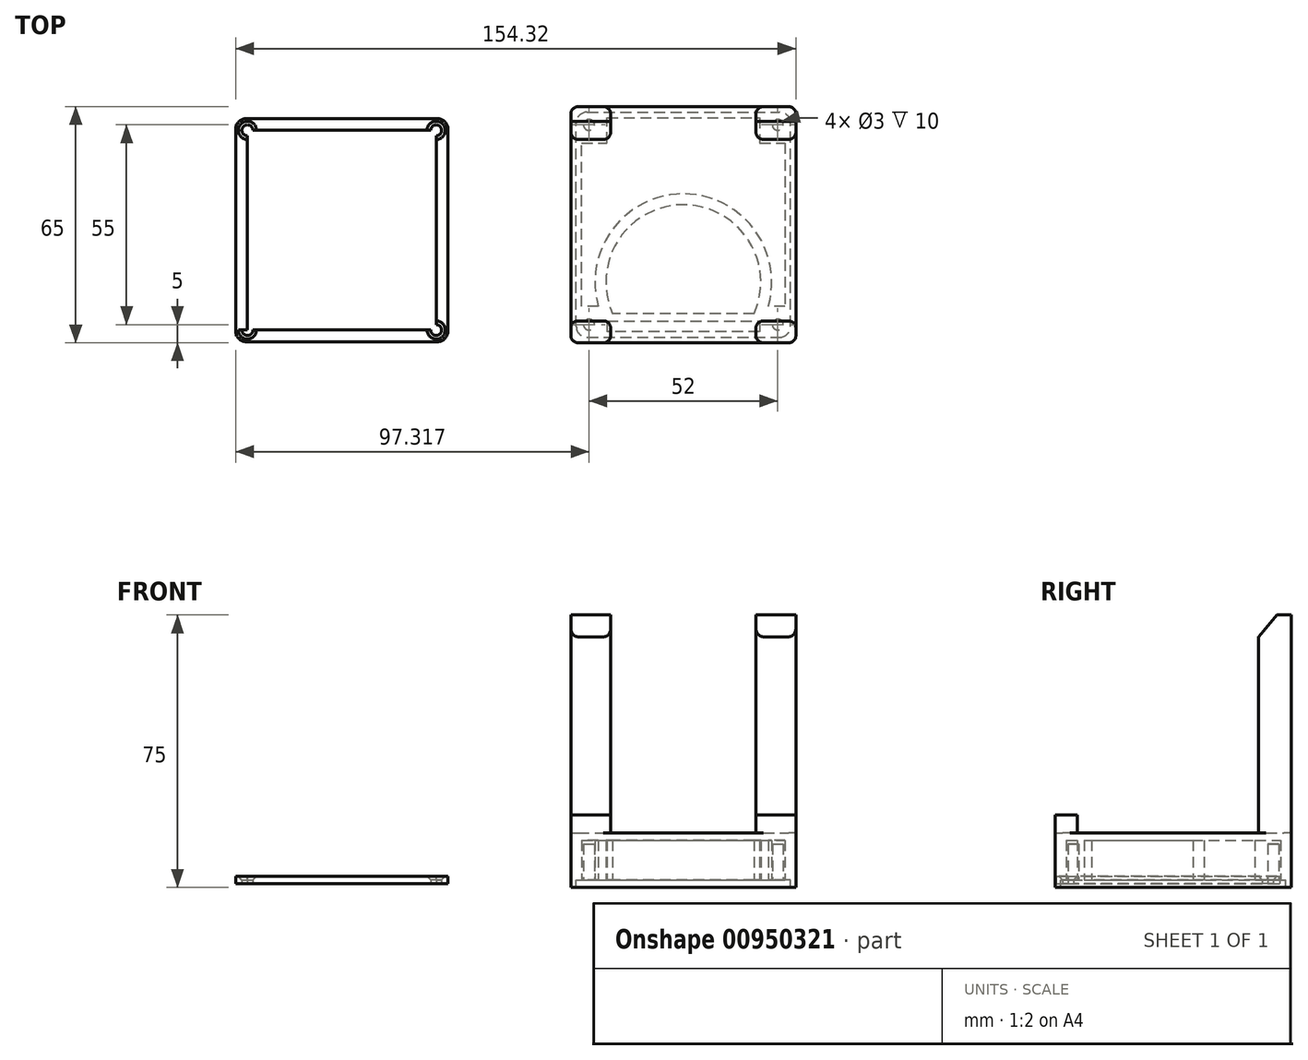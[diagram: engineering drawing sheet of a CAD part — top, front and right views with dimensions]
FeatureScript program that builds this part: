
annotation { "Feature Type Name" : "Feature", "Feature Type Description" : "" }
export const myFeature = defineFeature(function(context is Context, id is Id, definition is map)
    precondition{}
    {
        {
            var Q0;
            Q0=qCreatedBy(makeId("Top.planeOp"),FACE);
            var sketch = newSketch(context, id + "F0", { "sketchPlane" : qUnion([Q0])});
            skLineSegment(sketch, "E0.bottom", {"start": v(-55.57, -28) * mm, "end": v(-107.57, -28) * mm});
            skLineSegment(sketch, "E0.top", {"start": v(-55.57, 28) * mm, "end": v(-107.57, 28) * mm});
            skLineSegment(sketch, "E0.left", {"start": v(-50.57, -23) * mm, "end": v(-50.57, 23) * mm});
            skLineSegment(sketch, "E0.right", {"start": v(-112.57, -23) * mm, "end": v(-112.57, 23) * mm});
            skPoint(sketch, "E0.middle", {"position": v(-81.57, 0) * mm});
            skPoint(sketch, "E1.visualSharp", {"position": v(-112.57, 28) * mm});
            skPoint(sketch, "E2.visualSharp", {"position": v(-50.57, 28) * mm});
            skPoint(sketch, "E3.visualSharp", {"position": v(-50.57, -28) * mm});
            skPoint(sketch, "E4.visualSharp", {"position": v(-112.57, -28) * mm});
            skPoint(sketch, "E5", {"position": v(-81.57, -20) * mm});
            skPoint(sketch, "E5.positionSnap0", {"position": v(-81.57, -28) * mm});
            skPoint(sketch, "E6", {"position": v(-81.57, 10) * mm});
            skPoint(sketch, "E7", {"position": v(-101.07, -20) * mm});
            skPoint(sketch, "E8", {"position": v(-62.07, -20) * mm});
            skLineSegment(sketch, "E9", {"start": v(-101.07, -20) * mm, "end": v(-62.07, -20) * mm});
            skLineSegment(sketch, "E10", {"start": v(-81.57, 10) * mm, "end": v(-81.57, -20) * mm, "construction": true});
            skArc(sketch, "E11", {"start": v(-62.07, -20) * mm, "mid": v(-81.57, 10) * mm, "end": v(-101.07, -20) * mm});
            skLineSegment(sketch, "E12", {"start": v(-112.57, -23) * mm, "end": v(-112.57, -28) * mm});
            skLineSegment(sketch, "E13", {"start": v(-107.57, -28) * mm, "end": v(-112.57, -28) * mm});
            skLineSegment(sketch, "E14", {"start": v(-112.57, 23) * mm, "end": v(-112.57, 28) * mm});
            skLineSegment(sketch, "E15", {"start": v(-112.57, 28) * mm, "end": v(-107.57, 28) * mm});
            skLineSegment(sketch, "E16", {"start": v(-55.57, 28) * mm, "end": v(-50.57, 28) * mm});
            skLineSegment(sketch, "E17", {"start": v(-50.57, 28) * mm, "end": v(-50.57, 23) * mm});
            skLineSegment(sketch, "E18", {"start": v(-50.57, -23) * mm, "end": v(-50.57, -28) * mm});
            skLineSegment(sketch, "E19", {"start": v(-55.57, -28) * mm, "end": v(-50.57, -28) * mm});
            skArc(sketch, "E20.0", {"start": v(-60.21, -23) * mm, "mid": v(-81.57, 13) * mm, "end": v(-102.93, -23) * mm});
            skLineSegment(sketch, "E20.1", {"start": v(-102.93, -23) * mm, "end": v(-60.21, -23) * mm});
            skSolve(sketch);
        }
        {
            var Q0;
            Q0=makeQuery(id+"F0.imprint","IMPRINT",FACE,{"disambiguationData":[TD([[makeQuery(id+"F0.imprint","IMPRINT",EDGE,{"derivedFrom":sQuery(id+"F0.wireOp",EDGE,"E0.bottom")}),-1.0]])]});
            var Q1;
            Q1=makeQuery(id+"F0.imprint","IMPRINT",FACE,{"disambiguationData":[TD([[makeQuery(id+"F0.imprint","IMPRINT",EDGE,{"derivedFrom":sQuery(id+"F0.wireOp",EDGE,"E9")}),1.0]])]});
            var Q2;
            Q2=makeQuery(id+"F0.imprint","IMPRINT",FACE,{"disambiguationData":[TD([[makeQuery(id+"F0.imprint","IMPRINT",EDGE,{"derivedFrom":sQuery(id+"F0.wireOp",EDGE,"E9")}),-1.0]])]});
            extrude(context, id + "F1", {"entities" : qUnion([Q0, Q1, Q2]), "depth" : 14 * mm, "offsetDistance" : 25 * mm});
        }
        {
            var Q0;
            Q0=makeQuery(id+"F1.opExtrude","CAP_FACE",FACE,{"disambiguationData":[OSD([sQuery(id+"F0.wireOp",EDGE,"E0.bottom"),sQuery(id+"F0.wireOp",EDGE,"E0.top"),sQuery(id+"F0.wireOp",EDGE,"E0.left"),sQuery(id+"F0.wireOp",EDGE,"E0.right"),sQuery(id+"F0.wireOp",EDGE,"E12"),sQuery(id+"F0.wireOp",EDGE,"E13"),sQuery(id+"F0.wireOp",EDGE,"E14"),sQuery(id+"F0.wireOp",EDGE,"E15"),sQuery(id+"F0.wireOp",EDGE,"E16"),sQuery(id+"F0.wireOp",EDGE,"E17"),sQuery(id+"F0.wireOp",EDGE,"E18"),sQuery(id+"F0.wireOp",EDGE,"E19")])],"isStart":false});
            var sketch = newSketch(context, id + "F2", { "sketchPlane" : qUnion([Q0])});
            skLineSegment(sketch, "E21.bottom", {"start": v(-112.57, -28) * mm, "end": v(-101.57, -28) * mm});
            skLineSegment(sketch, "E21.top", {"start": v(-112.57, -25) * mm, "end": v(-101.57, -25) * mm});
            skLineSegment(sketch, "E21.left", {"start": v(-112.57, -28) * mm, "end": v(-112.57, -25) * mm});
            skLineSegment(sketch, "E21.right", {"start": v(-50.57, -28) * mm, "end": v(-50.57, -25) * mm});
            skLineSegment(sketch, "E22.bottom", {"start": v(-112.57, 28) * mm, "end": v(-101.57, 28) * mm});
            skLineSegment(sketch, "E22.top", {"start": v(-112.57, 25) * mm, "end": v(-101.57, 25) * mm});
            skLineSegment(sketch, "E22.left", {"start": v(-112.57, 28) * mm, "end": v(-112.57, 25) * mm});
            skLineSegment(sketch, "E22.right", {"start": v(-50.57, 28) * mm, "end": v(-50.57, 25) * mm});
            skPoint(sketch, "E23", {"position": v(-101.57, -25) * mm});
            skPoint(sketch, "E24", {"position": v(-61.57, -25) * mm});
            skPoint(sketch, "E25", {"position": v(-101.57, 25) * mm});
            skPoint(sketch, "E26", {"position": v(-61.57, 25) * mm});
            skLineSegment(sketch, "E27", {"start": v(-101.57, -25) * mm, "end": v(-101.57, -28) * mm});
            skLineSegment(sketch, "E28", {"start": v(-61.57, -25) * mm, "end": v(-61.57, -28) * mm});
            skLineSegment(sketch, "E29", {"start": v(-61.57, 25) * mm, "end": v(-61.57, 28) * mm});
            skLineSegment(sketch, "E30", {"start": v(-101.57, 25) * mm, "end": v(-101.57, 28) * mm});
            skLineSegment(sketch, "E31.trimOffspring", {"start": v(-61.57, -25) * mm, "end": v(-50.57, -25) * mm});
            skLineSegment(sketch, "E32.trimOffspring", {"start": v(-61.57, -28) * mm, "end": v(-50.57, -28) * mm});
            skLineSegment(sketch, "E33.trimOffspring", {"start": v(-61.57, 25) * mm, "end": v(-50.57, 25) * mm});
            skLineSegment(sketch, "E34.trimOffspring", {"start": v(-61.57, 28) * mm, "end": v(-50.57, 28) * mm});
            skSolve(sketch);
        }
        {
            var Q0;
            Q0=makeQuery(id+"F2.imprint","IMPRINT",FACE,{"disambiguationData":[TD([[makeQuery(id+"F2.imprint","IMPRINT",EDGE,{"derivedFrom":sQuery(id+"F2.wireOp",EDGE,"E21.bottom")}),-1.0]])]});
            var Q1;
            Q1=makeQuery(id+"F2.imprint","IMPRINT",FACE,{"disambiguationData":[TD([[makeQuery(id+"F2.imprint","IMPRINT",EDGE,{"derivedFrom":sQuery(id+"F2.wireOp",EDGE,"E21.right")}),-1.0]])]});
            extrude(context, id + "F3", {"entities" : qUnion([Q0, Q1]), "operationType" : NewBodyOperationType.ADD, "depth" : 5 * mm, "offsetDistance" : 25 * mm});
        }
        {
            var Q0;
            Q0=makeQuery(id+"F2.imprint","IMPRINT",FACE,{"disambiguationData":[TD([[makeQuery(id+"F2.imprint","IMPRINT",EDGE,{"derivedFrom":sQuery(id+"F2.wireOp",EDGE,"E22.bottom")}),-1.0]])]});
            var Q1;
            Q1=makeQuery(id+"F2.imprint","IMPRINT",FACE,{"disambiguationData":[TD([[makeQuery(id+"F2.imprint","IMPRINT",EDGE,{"derivedFrom":sQuery(id+"F2.wireOp",EDGE,"E22.right")}),-1.0]])]});
            extrude(context, id + "F4", {"entities" : qUnion([Q0, Q1]), "operationType" : NewBodyOperationType.ADD, "depth" : 60 * mm, "offsetDistance" : 25 * mm});
        }
        {
            var Q0;
            Q0=makeQuery(id+"F3.boolean.opBoolean","MERGE",FACE,{"derivedFrom":[makeQuery(id+"F1.opExtrude","SWEPT_FACE",FACE,{"disambiguationData":[OSD([sQuery(id+"F0.wireOp",EDGE,"E0.bottom"),sQuery(id+"F0.wireOp",EDGE,"E13"),sQuery(id+"F0.wireOp",EDGE,"E19")])]}),makeQuery(id+"F3.opExtrude","SWEPT_FACE",FACE,{"disambiguationData":[OSD([sQuery(id+"F2.wireOp",EDGE,"E21.bottom")])]}),makeQuery(id+"F3.opExtrude","SWEPT_FACE",FACE,{"disambiguationData":[OSD([sQuery(id+"F2.wireOp",EDGE,"E32.trimOffspring")])]})]});
            extrude(context, id + "F5", {"entities" : qUnion([Q0]), "operationType" : NewBodyOperationType.ADD, "depth" : 3 * mm, "offsetDistance" : 25 * mm});
        }
        {
            var Q0;
            Q0=makeQuery(id+"F4.boolean.opBoolean","MERGE",FACE,{"derivedFrom":[makeQuery(id+"F1.opExtrude","SWEPT_FACE",FACE,{"disambiguationData":[OSD([sQuery(id+"F0.wireOp",EDGE,"E0.top"),sQuery(id+"F0.wireOp",EDGE,"E15"),sQuery(id+"F0.wireOp",EDGE,"E16")])]}),makeQuery(id+"F4.opExtrude","SWEPT_FACE",FACE,{"disambiguationData":[OSD([sQuery(id+"F2.wireOp",EDGE,"E22.bottom")])]}),makeQuery(id+"F4.opExtrude","SWEPT_FACE",FACE,{"disambiguationData":[OSD([sQuery(id+"F2.wireOp",EDGE,"E34.trimOffspring")])]})]});
            extrude(context, id + "F6", {"entities" : qUnion([Q0]), "operationType" : NewBodyOperationType.ADD, "depth" : 6 * mm, "offsetDistance" : 25 * mm});
        }
        {
            var Q0;
            Q0=makeQuery(id+"F6.opExtrude","CAP_EDGE",EDGE,{"disambiguationData":[OSD([sQuery(id+"F0.wireOp",EDGE,"E16"),sQuery(id+"F0.wireOp",EDGE,"E17"),sQuery(id+"F2.wireOp",EDGE,"E22.right"),sQuery(id+"F2.wireOp",EDGE,"E34.trimOffspring")])],"isStart":false});
            var Q1;
            Q1=makeQuery(id+"F6.opExtrude","CAP_EDGE",EDGE,{"disambiguationData":[OSD([sQuery(id+"F0.wireOp",EDGE,"E0.top"),sQuery(id+"F0.wireOp",EDGE,"E15"),sQuery(id+"F0.wireOp",EDGE,"E16"),sQuery(id+"F2.wireOp",EDGE,"E29"),sQuery(id+"F2.wireOp",EDGE,"E34.trimOffspring")])],"isStart":false});
            var Q2;
            Q2=makeQuery(id+"F6.opExtrude","CAP_EDGE",EDGE,{"disambiguationData":[OSD([sQuery(id+"F0.wireOp",EDGE,"E0.top"),sQuery(id+"F0.wireOp",EDGE,"E15"),sQuery(id+"F0.wireOp",EDGE,"E16"),sQuery(id+"F2.wireOp",EDGE,"E22.bottom"),sQuery(id+"F2.wireOp",EDGE,"E30")])],"isStart":false});
            var Q3;
            Q3=makeQuery(id+"F6.opExtrude","CAP_EDGE",EDGE,{"disambiguationData":[OSD([sQuery(id+"F0.wireOp",EDGE,"E14"),sQuery(id+"F0.wireOp",EDGE,"E15"),sQuery(id+"F2.wireOp",EDGE,"E22.bottom"),sQuery(id+"F2.wireOp",EDGE,"E22.left")])],"isStart":false});
            var Q4;
            Q4=makeQuery(id+"F5.opExtrude","CAP_EDGE",EDGE,{"disambiguationData":[OSD([sQuery(id+"F0.wireOp",EDGE,"E18"),sQuery(id+"F0.wireOp",EDGE,"E19"),sQuery(id+"F2.wireOp",EDGE,"E21.right"),sQuery(id+"F2.wireOp",EDGE,"E32.trimOffspring")])],"isStart":false});
            var Q5;
            Q5=makeQuery(id+"F5.opExtrude","CAP_EDGE",EDGE,{"disambiguationData":[OSD([sQuery(id+"F0.wireOp",EDGE,"E12"),sQuery(id+"F0.wireOp",EDGE,"E13"),sQuery(id+"F2.wireOp",EDGE,"E21.bottom"),sQuery(id+"F2.wireOp",EDGE,"E21.left")])],"isStart":false});
            var Q6;
            Q6=makeQuery(id+"F5.opExtrude","CAP_EDGE",EDGE,{"disambiguationData":[OSD([sQuery(id+"F0.wireOp",EDGE,"E0.bottom"),sQuery(id+"F0.wireOp",EDGE,"E13"),sQuery(id+"F0.wireOp",EDGE,"E19"),sQuery(id+"F2.wireOp",EDGE,"E21.bottom"),sQuery(id+"F2.wireOp",EDGE,"E27")])],"isStart":false});
            var Q7;
            Q7=makeQuery(id+"F5.opExtrude","CAP_EDGE",EDGE,{"disambiguationData":[OSD([sQuery(id+"F0.wireOp",EDGE,"E0.bottom"),sQuery(id+"F0.wireOp",EDGE,"E13"),sQuery(id+"F0.wireOp",EDGE,"E19"),sQuery(id+"F2.wireOp",EDGE,"E28"),sQuery(id+"F2.wireOp",EDGE,"E32.trimOffspring")])],"isStart":false});
            fillet(context, id + "F7", {"entities" : qUnion([Q0, Q1, Q2, Q3, Q4, Q5, Q6, Q7]), "radius" : 2 * mm, "tangentPropagation" : true, "allowEdgeOverflow" : false});
        }
        {
            var Q0;
            Q0=makeQuery(id+"F3.opExtrude","SWEPT_EDGE",EDGE,{"disambiguationData":[OSD([sQuery(id+"F2.wireOp",EDGE,"E21.top"),sQuery(id+"F2.wireOp",EDGE,"E27")])]});
            var Q1;
            Q1=makeQuery(id+"F3.opExtrude","SWEPT_EDGE",EDGE,{"disambiguationData":[OSD([sQuery(id+"F0.wireOp",EDGE,"E0.right"),sQuery(id+"F0.wireOp",EDGE,"E12"),sQuery(id+"F0.wireOp",EDGE,"E14"),sQuery(id+"F2.wireOp",EDGE,"E21.top"),sQuery(id+"F2.wireOp",EDGE,"E21.left")])]});
            var Q2;
            Q2=makeQuery(id+"F3.opExtrude","SWEPT_EDGE",EDGE,{"disambiguationData":[OSD([sQuery(id+"F2.wireOp",EDGE,"E28"),sQuery(id+"F2.wireOp",EDGE,"E31.trimOffspring")])]});
            var Q3;
            Q3=makeQuery(id+"F3.opExtrude","SWEPT_EDGE",EDGE,{"disambiguationData":[OSD([sQuery(id+"F0.wireOp",EDGE,"E0.left"),sQuery(id+"F0.wireOp",EDGE,"E17"),sQuery(id+"F0.wireOp",EDGE,"E18"),sQuery(id+"F2.wireOp",EDGE,"E21.right"),sQuery(id+"F2.wireOp",EDGE,"E31.trimOffspring")])]});
            fillet(context, id + "F8", {"entities" : qUnion([Q0, Q1, Q2, Q3]), "radius" : 2 * mm, "tangentPropagation" : true, "allowEdgeOverflow" : false});
        }
        {
            var Q0;
            Q0=makeQuery(id+"F4.opExtrude","CAP_EDGE",EDGE,{"disambiguationData":[OSD([sQuery(id+"F2.wireOp",EDGE,"E22.top")])],"isStart":false});
            var Q1;
            Q1=makeQuery(id+"F4.opExtrude","CAP_EDGE",EDGE,{"disambiguationData":[OSD([sQuery(id+"F2.wireOp",EDGE,"E33.trimOffspring")])],"isStart":false});
            chamfer(context, id + "F9", {"entities" : qUnion([Q0, Q1]), "chamferType" : ChamferType.TWO_OFFSETS, "width1" : 5 * mm, "oppositeDirection" : false, "width2" : 6 * mm, "tangentPropagation" : true});
        }
        {
            var Q0;
            Q0=makeQuery(id+"F4.opExtrude","SWEPT_EDGE",EDGE,{"disambiguationData":[OSD([sQuery(id+"F2.wireOp",EDGE,"E22.top"),sQuery(id+"F2.wireOp",EDGE,"E30")])]});
            var Q1;
            Q1=makeQuery(id+"F4.opExtrude","SWEPT_EDGE",EDGE,{"disambiguationData":[OSD([sQuery(id+"F0.wireOp",EDGE,"E0.right"),sQuery(id+"F0.wireOp",EDGE,"E12"),sQuery(id+"F0.wireOp",EDGE,"E14"),sQuery(id+"F2.wireOp",EDGE,"E22.top"),sQuery(id+"F2.wireOp",EDGE,"E22.left")])]});
            var Q2;
            Q2=makeQuery(id+"F4.opExtrude","SWEPT_EDGE",EDGE,{"disambiguationData":[OSD([sQuery(id+"F2.wireOp",EDGE,"E29"),sQuery(id+"F2.wireOp",EDGE,"E33.trimOffspring")])]});
            var Q3;
            Q3=makeQuery(id+"F4.opExtrude","SWEPT_EDGE",EDGE,{"disambiguationData":[OSD([sQuery(id+"F0.wireOp",EDGE,"E0.left"),sQuery(id+"F0.wireOp",EDGE,"E17"),sQuery(id+"F0.wireOp",EDGE,"E18"),sQuery(id+"F2.wireOp",EDGE,"E22.right"),sQuery(id+"F2.wireOp",EDGE,"E33.trimOffspring")])]});
            fillet(context, id + "F10", {"entities" : qUnion([Q0, Q1, Q2, Q3]), "radius" : 2 * mm, "tangentPropagation" : true, "allowEdgeOverflow" : false});
        }
        {
            var Q0;
            {var subQ0=sQuery(id+"F0.wireOp",EDGE,"E16");var subQ1=sQuery(id+"F0.wireOp",EDGE,"E15");var subQ2=sQuery(id+"F0.wireOp",EDGE,"E0.top");var subQ3=sQuery(id+"F0.wireOp",EDGE,"E19");var subQ4=sQuery(id+"F0.wireOp",EDGE,"E13");var subQ5=sQuery(id+"F0.wireOp",EDGE,"E0.bottom");Q0=makeQuery(id+"F6.boolean.opBoolean","MERGE",FACE,{"derivedFrom":[makeQuery(id+"F5.boolean.opBoolean","MERGE",FACE,{"derivedFrom":[makeQuery(id+"F1.opExtrude","CAP_FACE",FACE,{"disambiguationData":[OSD([subQ5,subQ2,sQuery(id+"F0.wireOp",EDGE,"E0.left"),sQuery(id+"F0.wireOp",EDGE,"E0.right"),sQuery(id+"F0.wireOp",EDGE,"E12"),subQ4,sQuery(id+"F0.wireOp",EDGE,"E14"),subQ1,subQ0,sQuery(id+"F0.wireOp",EDGE,"E17"),sQuery(id+"F0.wireOp",EDGE,"E18"),subQ3])],"isStart":true}),makeQuery(id+"F5.opExtrude","SWEPT_FACE",FACE,{"disambiguationData":[OSD([subQ5,subQ4,subQ3]),TDD([makeQuery(id+"F1.opExtrude","CAP_EDGE",EDGE,{"disambiguationData":[OSD([subQ5,subQ4,subQ3])],"isStart":true})])]})]}),makeQuery(id+"F6.opExtrude","SWEPT_FACE",FACE,{"disambiguationData":[OSD([subQ2,subQ1,subQ0]),TDD([makeQuery(id+"F1.opExtrude","CAP_EDGE",EDGE,{"disambiguationData":[OSD([subQ2,subQ1,subQ0])],"isStart":true})])]})]});}
            var sketch = newSketch(context, id + "F11", { "sketchPlane" : qUnion([Q0])});
            skPoint(sketch, "E35", {"position": v(-81.57, 23) * mm});
            skPoint(sketch, "E35.positionSnap0", {"position": v(-81.57, 31) * mm});
            skPoint(sketch, "E36", {"position": v(-81.57, -7) * mm});
            skPoint(sketch, "E37", {"position": v(-101.07, 23) * mm});
            skPoint(sketch, "E38", {"position": v(-62.07, 23) * mm});
            skLineSegment(sketch, "E39", {"start": v(-81.57, 23) * mm, "end": v(-101.07, 23) * mm});
            skLineSegment(sketch, "E40", {"start": v(-81.57, 23) * mm, "end": v(-62.07, 23) * mm});
            skLineSegment(sketch, "E41", {"start": v(-81.57, -7) * mm, "end": v(-81.57, 23) * mm});
            skArc(sketch, "E42", {"start": v(-101.07, 23) * mm, "mid": v(-81.57, -7) * mm, "end": v(-62.07, 23) * mm});
            skLineSegment(sketch, "E43.0", {"start": v(-60.57, 28) * mm, "end": v(-102.57, 28) * mm});
            skLineSegment(sketch, "E43.1", {"start": v(-53.57, -24) * mm, "end": v(-53.57, 21) * mm});
            skLineSegment(sketch, "E43.2", {"start": v(-102.57, -31) * mm, "end": v(-60.57, -31) * mm});
            skLineSegment(sketch, "E43.3", {"start": v(-109.57, 21) * mm, "end": v(-109.57, -24) * mm});
            skPoint(sketch, "E44", {"position": v(-102.57, -31) * mm});
            skPoint(sketch, "E45", {"position": v(-109.57, -24) * mm});
            skPoint(sketch, "E46", {"position": v(-60.57, -31) * mm});
            skPoint(sketch, "E47", {"position": v(-53.57, -24) * mm});
            skPoint(sketch, "E48", {"position": v(-60.57, 28) * mm});
            skPoint(sketch, "E49", {"position": v(-53.57, 21) * mm});
            skPoint(sketch, "E50", {"position": v(-109.57, 21) * mm});
            skPoint(sketch, "E51", {"position": v(-102.57, 28) * mm});
            skLineSegment(sketch, "E52", {"start": v(-112.57, -24) * mm, "end": v(-102.57, -24) * mm});
            skLineSegment(sketch, "E53", {"start": v(-102.57, -24) * mm, "end": v(-102.57, -34) * mm});
            skLineSegment(sketch, "E54", {"start": v(-60.57, -34) * mm, "end": v(-60.57, -24) * mm});
            skLineSegment(sketch, "E55", {"start": v(-60.57, -24) * mm, "end": v(-50.57, -24) * mm});
            skLineSegment(sketch, "E56", {"start": v(-50.57, 21) * mm, "end": v(-58.16, 21) * mm});
            skLineSegment(sketch, "E57", {"start": v(-60.57, 26) * mm, "end": v(-60.57, 31) * mm});
            skLineSegment(sketch, "E58", {"start": v(-102.57, 31) * mm, "end": v(-102.57, 26) * mm});
            skLineSegment(sketch, "E59", {"start": v(-104.98, 21) * mm, "end": v(-112.57, 21) * mm});
            skArc(sketch, "E60.0", {"start": v(-104.98, 21) * mm, "mid": v(-81.57, -10) * mm, "end": v(-58.16, 21) * mm});
            skPoint(sketch, "E61.orphan", {"position": v(-102.57, 21) * mm});
            skPoint(sketch, "E62.orphan", {"position": v(-60.57, 21) * mm});
            skLineSegment(sketch, "E63.0", {"start": v(-81.57, 25) * mm, "end": v(-102.57, 25) * mm});
            skLineSegment(sketch, "E63.1", {"start": v(-81.57, 25) * mm, "end": v(-60.57, 25) * mm});
            skLineSegment(sketch, "E64", {"start": v(-102.57, 25) * mm, "end": v(-102.57, 26) * mm});
            skLineSegment(sketch, "E65", {"start": v(-60.57, 25) * mm, "end": v(-60.57, 26) * mm});
            skLineSegment(sketch, "E66", {"start": v(-102.57, 31) * mm, "end": v(-60.57, 31) * mm});
            skLineSegment(sketch, "E67", {"start": v(-50.57, 21) * mm, "end": v(-50.57, -24) * mm});
            skLineSegment(sketch, "E68", {"start": v(-60.57, -34) * mm, "end": v(-102.57, -34) * mm});
            skLineSegment(sketch, "E69", {"start": v(-112.57, -24) * mm, "end": v(-112.57, 21) * mm});
            skPoint(sketch, "E70", {"position": v(-112.57, 26) * mm});
            skPoint(sketch, "E71", {"position": v(-107.57, 31) * mm});
            skPoint(sketch, "E72", {"position": v(-112.57, -29) * mm});
            skPoint(sketch, "E73", {"position": v(-107.57, -34) * mm});
            skPoint(sketch, "E74", {"position": v(-55.57, -34) * mm});
            skPoint(sketch, "E75", {"position": v(-50.57, -29) * mm});
            skPoint(sketch, "E76", {"position": v(-50.57, 26) * mm});
            skPoint(sketch, "E77", {"position": v(-55.57, 31) * mm});
            skPoint(sketch, "E78", {"position": v(-107.57, -29) * mm});
            skPoint(sketch, "E79", {"position": v(-55.57, -29) * mm});
            skPoint(sketch, "E80", {"position": v(-55.57, 26) * mm});
            skPoint(sketch, "E81", {"position": v(-107.57, 26) * mm});
            skCircle(sketch, "E82", {"center": v(-107.57, 26) * mm, "radius": 1.5 * mm});
            skCircle(sketch, "E83", {"center": v(-55.57, 26) * mm, "radius": 1.5 * mm});
            skCircle(sketch, "E84", {"center": v(-107.57, -29) * mm, "radius": 1.5 * mm});
            skCircle(sketch, "E85", {"center": v(-55.57, -29) * mm, "radius": 1.5 * mm});
            skPoint(sketch, "E86", {"position": v(-111.07, 21) * mm});
            skPoint(sketch, "E87", {"position": v(-102.57, 29.5) * mm});
            skPoint(sketch, "E88", {"position": v(-60.57, -32.5) * mm});
            skPoint(sketch, "E89", {"position": v(-52.07, -24) * mm});
            skLineSegment(sketch, "E90", {"start": v(-60.57, -32.5) * mm, "end": v(-102.57, -32.5) * mm});
            skLineSegment(sketch, "E91", {"start": v(-111.07, 21) * mm, "end": v(-111.07, -24) * mm});
            skLineSegment(sketch, "E92", {"start": v(-52.07, -24) * mm, "end": v(-52.07, 21) * mm});
            skLineSegment(sketch, "E93", {"start": v(-102.57, 29.5) * mm, "end": v(-60.57, 29.5) * mm});
            skLineSegment(sketch, "E94", {"start": v(-60.57, 29.5) * mm, "end": v(-55.07, 29.5) * mm});
            skLineSegment(sketch, "E95", {"start": v(-52.07, 26.5) * mm, "end": v(-52.07, 21) * mm});
            skLineSegment(sketch, "E96", {"start": v(-102.57, 29.5) * mm, "end": v(-108.07, 29.5) * mm});
            skLineSegment(sketch, "E97", {"start": v(-111.07, 26.5) * mm, "end": v(-111.07, 21) * mm});
            skLineSegment(sketch, "E98", {"start": v(-111.07, -24) * mm, "end": v(-111.07, -29.5) * mm});
            skLineSegment(sketch, "E99", {"start": v(-108.07, -32.5) * mm, "end": v(-102.57, -32.5) * mm});
            skPoint(sketch, "E100.visualSharp", {"position": v(-111.07, -32.5) * mm});
            skArc(sketch, "E100.filletArc", {"start": v(-111.07, -29.5) * mm, "mid": v(-110.2, -31.62) * mm, "end": v(-108.07, -32.5) * mm});
            skLineSegment(sketch, "E101", {"start": v(-60.57, -32.5) * mm, "end": v(-55.07, -32.5) * mm});
            skLineSegment(sketch, "E102", {"start": v(-52.07, -29.5) * mm, "end": v(-52.07, -24) * mm});
            skPoint(sketch, "E103.visualSharp", {"position": v(-52.07, -32.5) * mm});
            skArc(sketch, "E103.filletArc", {"start": v(-55.07, -32.5) * mm, "mid": v(-52.95, -31.62) * mm, "end": v(-52.07, -29.5) * mm});
            skPoint(sketch, "E104.visualSharp", {"position": v(-52.07, 29.5) * mm});
            skArc(sketch, "E104.filletArc", {"start": v(-52.07, 26.5) * mm, "mid": v(-52.95, 28.62) * mm, "end": v(-55.07, 29.5) * mm});
            skPoint(sketch, "E105.visualSharp", {"position": v(-111.07, 29.5) * mm});
            skArc(sketch, "E105.filletArc", {"start": v(-108.07, 29.5) * mm, "mid": v(-110.2, 28.62) * mm, "end": v(-111.07, 26.5) * mm});
            skSolve(sketch);
        }
        {
            var Q0;
            {var subQ0=sQuery(id+"F11.wireOp",EDGE,"E39");Q0=makeQuery(id+"F11.imprint","IMPRINT",FACE,{"disambiguationData":[TD([[makeQuery(id+"F11.imprint","IMPRINT",EDGE,{"derivedFrom":subQ0}),1.0]])]});}
            var Q1;
            {var subQ0=sQuery(id+"F11.wireOp",EDGE,"E40");Q1=makeQuery(id+"F11.imprint","IMPRINT",FACE,{"disambiguationData":[TD([[makeQuery(id+"F11.imprint","IMPRINT",EDGE,{"derivedFrom":subQ0}),-1.0]])]});}
            var Q2;
            {var subQ1=sQuery(id+"F11.wireOp",EDGE,"E43.0");Q2=makeQuery(id+"F11.imprint","IMPRINT",FACE,{"disambiguationData":[TD([[makeQuery(id+"F11.imprint","IMPRINT",EDGE,{"derivedFrom":subQ1}),1.0]])]});}
            var Q3;
            {var subQ6=sQuery(id+"F11.wireOp",EDGE,"E43.1");Q3=makeQuery(id+"F11.imprint","IMPRINT",FACE,{"disambiguationData":[TD([[makeQuery(id+"F11.imprint","IMPRINT",EDGE,{"derivedFrom":subQ6}),1.0]])]});}
            extrude(context, id + "F12", {"entities" : qUnion([Q0, Q1, Q2, Q3]), "operationType" : NewBodyOperationType.REMOVE, "oppositeDirection" : true, "depth" : 12 * mm, "offsetDistance" : 25 * mm});
        }
        {
            var Q0;
            Q0=makeQuery(id+"F11.imprint","IMPRINT",FACE,{"disambiguationData":[TD([[makeQuery(id+"F11.imprint","IMPRINT",EDGE,{"derivedFrom":sQuery(id+"F11.wireOp",EDGE,"E82")}),1.0]])]});
            var Q1;
            Q1=makeQuery(id+"F11.imprint","IMPRINT",FACE,{"disambiguationData":[TD([[makeQuery(id+"F11.imprint","IMPRINT",EDGE,{"derivedFrom":sQuery(id+"F11.wireOp",EDGE,"E83")}),1.0]])]});
            var Q2;
            Q2=makeQuery(id+"F11.imprint","IMPRINT",FACE,{"disambiguationData":[TD([[makeQuery(id+"F11.imprint","IMPRINT",EDGE,{"derivedFrom":sQuery(id+"F11.wireOp",EDGE,"E85")}),1.0]])]});
            var Q3;
            Q3=makeQuery(id+"F11.imprint","IMPRINT",FACE,{"disambiguationData":[TD([[makeQuery(id+"F11.imprint","IMPRINT",EDGE,{"derivedFrom":sQuery(id+"F11.wireOp",EDGE,"E84")}),1.0]])]});
            extrude(context, id + "F13", {"entities" : qUnion([Q0, Q1, Q2, Q3]), "operationType" : NewBodyOperationType.REMOVE, "oppositeDirection" : true, "depth" : 11 * mm, "offsetDistance" : 25 * mm});
        }
        {
            var Q0;
            {var subQ1=sQuery(id+"F11.wireOp",EDGE,"E96");Q0=makeQuery(id+"F11.imprint","IMPRINT",FACE,{"disambiguationData":[TD([[makeQuery(id+"F11.imprint","IMPRINT",EDGE,{"derivedFrom":subQ1}),-1.0]])]});}
            var Q1;
            {var subQ0=sQuery(id+"F11.wireOp",EDGE,"E69");Q1=makeQuery(id+"F11.imprint","IMPRINT",FACE,{"disambiguationData":[TD([[makeQuery(id+"F11.imprint","IMPRINT",EDGE,{"derivedFrom":subQ0}),1.0]])]});}
            var Q2;
            {var subQ0=sQuery(id+"F11.wireOp",EDGE,"E66");Q2=makeQuery(id+"F11.imprint","IMPRINT",FACE,{"disambiguationData":[TD([[makeQuery(id+"F11.imprint","IMPRINT",EDGE,{"derivedFrom":subQ0}),1.0]])]});}
            var Q3;
            {var subQ0=sQuery(id+"F11.wireOp",EDGE,"E94");Q3=makeQuery(id+"F11.imprint","IMPRINT",FACE,{"disambiguationData":[TD([[makeQuery(id+"F11.imprint","IMPRINT",EDGE,{"derivedFrom":subQ0}),1.0]])]});}
            var Q4;
            {var subQ0=sQuery(id+"F11.wireOp",EDGE,"E67");Q4=makeQuery(id+"F11.imprint","IMPRINT",FACE,{"disambiguationData":[TD([[makeQuery(id+"F11.imprint","IMPRINT",EDGE,{"derivedFrom":subQ0}),1.0]])]});}
            var Q5;
            {var subQ15=sQuery(id+"F11.wireOp",EDGE,"E101");Q5=makeQuery(id+"F11.imprint","IMPRINT",FACE,{"disambiguationData":[TD([[makeQuery(id+"F11.imprint","IMPRINT",EDGE,{"derivedFrom":subQ15}),-1.0]])]});}
            var Q6;
            {var subQ0=sQuery(id+"F11.wireOp",EDGE,"E68");Q6=makeQuery(id+"F11.imprint","IMPRINT",FACE,{"disambiguationData":[TD([[makeQuery(id+"F11.imprint","IMPRINT",EDGE,{"derivedFrom":subQ0}),1.0]])]});}
            var Q7;
            {var subQ1=sQuery(id+"F11.wireOp",EDGE,"E98");Q7=makeQuery(id+"F11.imprint","IMPRINT",FACE,{"disambiguationData":[TD([[makeQuery(id+"F11.imprint","IMPRINT",EDGE,{"derivedFrom":subQ1}),-1.0]])]});}
            extrude(context, id + "F14", {"entities" : qUnion([Q0, Q1, Q2, Q3, Q4, Q5, Q6, Q7]), "operationType" : NewBodyOperationType.ADD, "depth" : 1 * mm, "offsetDistance" : 25 * mm});
        }
        {
            var Q0;
            {var subQ8=sQuery(id+"F11.wireOp",EDGE,"E39");Q0=makeQuery(id+"F11.imprint","IMPRINT",FACE,{"disambiguationData":[TD([[makeQuery(id+"F11.imprint","IMPRINT",EDGE,{"derivedFrom":subQ8}),-1.0]])]});}
            var Q1;
            {var subQ0=sQuery(id+"F11.wireOp",EDGE,"E43.0");Q1=makeQuery(id+"F11.imprint","IMPRINT",FACE,{"disambiguationData":[TD([[makeQuery(id+"F11.imprint","IMPRINT",EDGE,{"derivedFrom":subQ0}),-1.0]])]});}
            var Q2;
            {var subQ0=sQuery(id+"F11.wireOp",EDGE,"E43.3");Q2=makeQuery(id+"F11.imprint","IMPRINT",FACE,{"disambiguationData":[TD([[makeQuery(id+"F11.imprint","IMPRINT",EDGE,{"derivedFrom":subQ0}),-1.0]])]});}
            var Q3;
            {var subQ0=sQuery(id+"F11.wireOp",EDGE,"E43.1");Q3=makeQuery(id+"F11.imprint","IMPRINT",FACE,{"disambiguationData":[TD([[makeQuery(id+"F11.imprint","IMPRINT",EDGE,{"derivedFrom":subQ0}),-1.0]])]});}
            var Q4;
            Q4=makeQuery(id+"F11.imprint","IMPRINT",FACE,{"disambiguationData":[TD([[makeQuery(id+"F11.imprint","IMPRINT",EDGE,{"derivedFrom":sQuery(id+"F11.wireOp",EDGE,"E85")}),-1.0]])]});
            var Q5;
            Q5=makeQuery(id+"F11.imprint","IMPRINT",FACE,{"disambiguationData":[TD([[makeQuery(id+"F11.imprint","IMPRINT",EDGE,{"derivedFrom":sQuery(id+"F11.wireOp",EDGE,"E84")}),-1.0]])]});
            var Q6;
            {var subQ0=sQuery(id+"F11.wireOp",EDGE,"E43.2");Q6=makeQuery(id+"F11.imprint","IMPRINT",FACE,{"disambiguationData":[TD([[makeQuery(id+"F11.imprint","IMPRINT",EDGE,{"derivedFrom":subQ0}),-1.0]])]});}
            extrude(context, id + "F15", {"entities" : qUnion([Q0, Q1, Q2, Q3, Q4, Q5, Q6]), "operationType" : NewBodyOperationType.REMOVE, "oppositeDirection" : true, "depth" : 1 * mm, "offsetDistance" : 25 * mm});
        }
        {
            var Q0;
            Q0=qCreatedBy(makeId("Top.planeOp"),FACE);
            var sketch = newSketch(context, id + "F16", { "sketchPlane" : qUnion([Q0])});
            skLineSegment(sketch, "E106.bottom", {"start": v(-149.4, -30.75) * mm, "end": v(-201.9, -30.75) * mm});
            skLineSegment(sketch, "E106.top", {"start": v(-149.4, 30.75) * mm, "end": v(-201.9, 30.75) * mm});
            skLineSegment(sketch, "E106.left", {"start": v(-146.4, -27.75) * mm, "end": v(-146.4, 27.75) * mm});
            skLineSegment(sketch, "E106.right", {"start": v(-204.9, -27.75) * mm, "end": v(-204.9, 27.75) * mm});
            skPoint(sketch, "E106.middle", {"position": v(-175.64, 0) * mm});
            skPoint(sketch, "E107", {"position": v(-201.64, -30.75) * mm});
            skPoint(sketch, "E108", {"position": v(-204.9, -27.5) * mm});
            skPoint(sketch, "E109", {"position": v(-146.4, 27.5) * mm});
            skPoint(sketch, "E110", {"position": v(-149.64, 30.75) * mm});
            skLineSegment(sketch, "E111", {"start": v(-204.9, -27.5) * mm, "end": v(-146.4, -27.5) * mm});
            skLineSegment(sketch, "E112", {"start": v(-201.64, -30.75) * mm, "end": v(-201.64, 30.75) * mm});
            skLineSegment(sketch, "E113", {"start": v(-149.64, 30.75) * mm, "end": v(-149.64, -30.75) * mm});
            skLineSegment(sketch, "E114", {"start": v(-146.4, 27.5) * mm, "end": v(-204.9, 27.5) * mm});
            skPoint(sketch, "E115.visualSharp", {"position": v(-204.9, -30.75) * mm});
            skArc(sketch, "E115.filletArc", {"start": v(-204.9, -27.75) * mm, "mid": v(-204.02, -29.87) * mm, "end": v(-201.9, -30.75) * mm});
            skPoint(sketch, "E116.visualSharp", {"position": v(-146.4, -30.75) * mm});
            skArc(sketch, "E116.filletArc", {"start": v(-149.4, -30.75) * mm, "mid": v(-147.27, -29.87) * mm, "end": v(-146.4, -27.75) * mm});
            skPoint(sketch, "E117.visualSharp", {"position": v(-146.4, 30.75) * mm});
            skArc(sketch, "E117.filletArc", {"start": v(-146.4, 27.75) * mm, "mid": v(-147.27, 29.87) * mm, "end": v(-149.4, 30.75) * mm});
            skPoint(sketch, "E118.visualSharp", {"position": v(-204.9, 30.75) * mm});
            skArc(sketch, "E118.filletArc", {"start": v(-201.9, 30.75) * mm, "mid": v(-204.02, 29.87) * mm, "end": v(-204.9, 27.75) * mm});
            skCircle(sketch, "E119", {"center": v(-149.64, -27.5) * mm, "radius": 1.5 * mm});
            skCircle(sketch, "E120", {"center": v(-201.64, -27.5) * mm, "radius": 1.5 * mm});
            skCircle(sketch, "E121", {"center": v(-201.64, 27.5) * mm, "radius": 1.5 * mm});
            skCircle(sketch, "E122", {"center": v(-149.64, 27.5) * mm, "radius": 1.5 * mm});
            skSolve(sketch);
        }
        {
            var Q0;
            {var subQ5=sQuery(id+"F16.wireOp",EDGE,"E115.filletArc");Q0=makeQuery(id+"F16.imprint","IMPRINT",FACE,{"disambiguationData":[TD([[makeQuery(id+"F16.imprint","IMPRINT",EDGE,{"derivedFrom":subQ5}),1.0]])]});}
            var Q1;
            {var subQ5=sQuery(id+"F16.wireOp",EDGE,"E118.filletArc");Q1=makeQuery(id+"F16.imprint","IMPRINT",FACE,{"disambiguationData":[TD([[makeQuery(id+"F16.imprint","IMPRINT",EDGE,{"derivedFrom":subQ5}),1.0]])]});}
            var Q2;
            {var subQ9=sQuery(id+"F16.wireOp",EDGE,"E120");var subQ13=sQuery(id+"F16.wireOp",EDGE,"E111");var subQ14=makeQuery(id+"F16.imprint","INTERSECT",VERTEX,{"disambiguationData":[OD(1.0)],"derivedFrom":[subQ13,subQ9]});Q2=makeQuery(id+"F16.imprint","IMPRINT",FACE,{"disambiguationData":[TD([[makeQuery(id+"F16.imprint","IMPRINT",EDGE,{"disambiguationData":[TD([[subQ14,-1.0]])],"derivedFrom":subQ13}),1.0]])]});}
            var Q3;
            {var subQ5=sQuery(id+"F16.wireOp",EDGE,"E111");var subQ6=sQuery(id+"F16.wireOp",EDGE,"E106.left");var subQ7=makeQuery(id+"F16.imprint","INTERSECT",VERTEX,{"derivedFrom":[subQ6,subQ5]});Q3=makeQuery(id+"F16.imprint","IMPRINT",FACE,{"disambiguationData":[TD([[makeQuery(id+"F16.imprint","IMPRINT",EDGE,{"disambiguationData":[TD([[subQ7,-1.0]])],"derivedFrom":subQ6}),1.0]])]});}
            var Q4;
            {var subQ1=sQuery(id+"F16.wireOp",EDGE,"E106.bottom");var subQ5=sQuery(id+"F16.wireOp",EDGE,"E112");var subQ6=makeQuery(id+"F16.imprint","INTERSECT",VERTEX,{"derivedFrom":[subQ1,subQ5]});Q4=makeQuery(id+"F16.imprint","IMPRINT",FACE,{"disambiguationData":[TD([[makeQuery(id+"F16.imprint","IMPRINT",EDGE,{"disambiguationData":[TD([[subQ6,1.0]])],"derivedFrom":subQ1}),-1.0]])]});}
            var Q5;
            {var subQ1=sQuery(id+"F16.wireOp",EDGE,"E106.right");var subQ9=sQuery(id+"F16.wireOp",EDGE,"E111");var subQ10=makeQuery(id+"F16.imprint","INTERSECT",VERTEX,{"derivedFrom":[subQ1,subQ9]});Q5=makeQuery(id+"F16.imprint","IMPRINT",FACE,{"disambiguationData":[TD([[makeQuery(id+"F16.imprint","IMPRINT",EDGE,{"disambiguationData":[TD([[subQ10,-1.0]])],"derivedFrom":subQ1}),-1.0]])]});}
            var Q6;
            {var subQ5=sQuery(id+"F16.wireOp",EDGE,"E112");var subQ6=sQuery(id+"F16.wireOp",EDGE,"E106.top");var subQ7=makeQuery(id+"F16.imprint","INTERSECT",VERTEX,{"derivedFrom":[subQ6,subQ5]});Q6=makeQuery(id+"F16.imprint","IMPRINT",FACE,{"disambiguationData":[TD([[makeQuery(id+"F16.imprint","IMPRINT",EDGE,{"disambiguationData":[TD([[subQ7,1.0]])],"derivedFrom":subQ6}),1.0]])]});}
            var Q7;
            {var subQ9=sQuery(id+"F16.wireOp",EDGE,"E116.filletArc");Q7=makeQuery(id+"F16.imprint","IMPRINT",FACE,{"disambiguationData":[TD([[makeQuery(id+"F16.imprint","IMPRINT",EDGE,{"derivedFrom":subQ9}),1.0]])]});}
            var Q8;
            {var subQ9=sQuery(id+"F16.wireOp",EDGE,"E117.filletArc");Q8=makeQuery(id+"F16.imprint","IMPRINT",FACE,{"disambiguationData":[TD([[makeQuery(id+"F16.imprint","IMPRINT",EDGE,{"derivedFrom":subQ9}),1.0]])]});}
            extrude(context, id + "F17", {"entities" : qUnion([Q0, Q1, Q2, Q3, Q4, Q5, Q6, Q7, Q8]), "depth" : 2 * mm, "offsetDistance" : 25 * mm});
        }
        {
            var Q0;
            Q0=makeQuery(id+"F17.opExtrude","CAP_EDGE",EDGE,{"disambiguationData":[OSD([sQuery(id+"F16.wireOp",EDGE,"E121")])],"isStart":false});
            var Q1;
            Q1=makeQuery(id+"F17.opExtrude","CAP_EDGE",EDGE,{"disambiguationData":[OSD([sQuery(id+"F16.wireOp",EDGE,"E122")])],"isStart":false});
            var Q2;
            Q2=makeQuery(id+"F17.opExtrude","CAP_EDGE",EDGE,{"disambiguationData":[OSD([sQuery(id+"F16.wireOp",EDGE,"E119")])],"isStart":false});
            var Q3;
            Q3=makeQuery(id+"F17.opExtrude","CAP_EDGE",EDGE,{"disambiguationData":[OSD([sQuery(id+"F16.wireOp",EDGE,"E120")])],"isStart":false});
            chamfer(context, id + "F18", {"entities" : qUnion([Q0, Q1, Q2, Q3]), "width" : 1 * mm, "tangentPropagation" : true});
        }
    });
